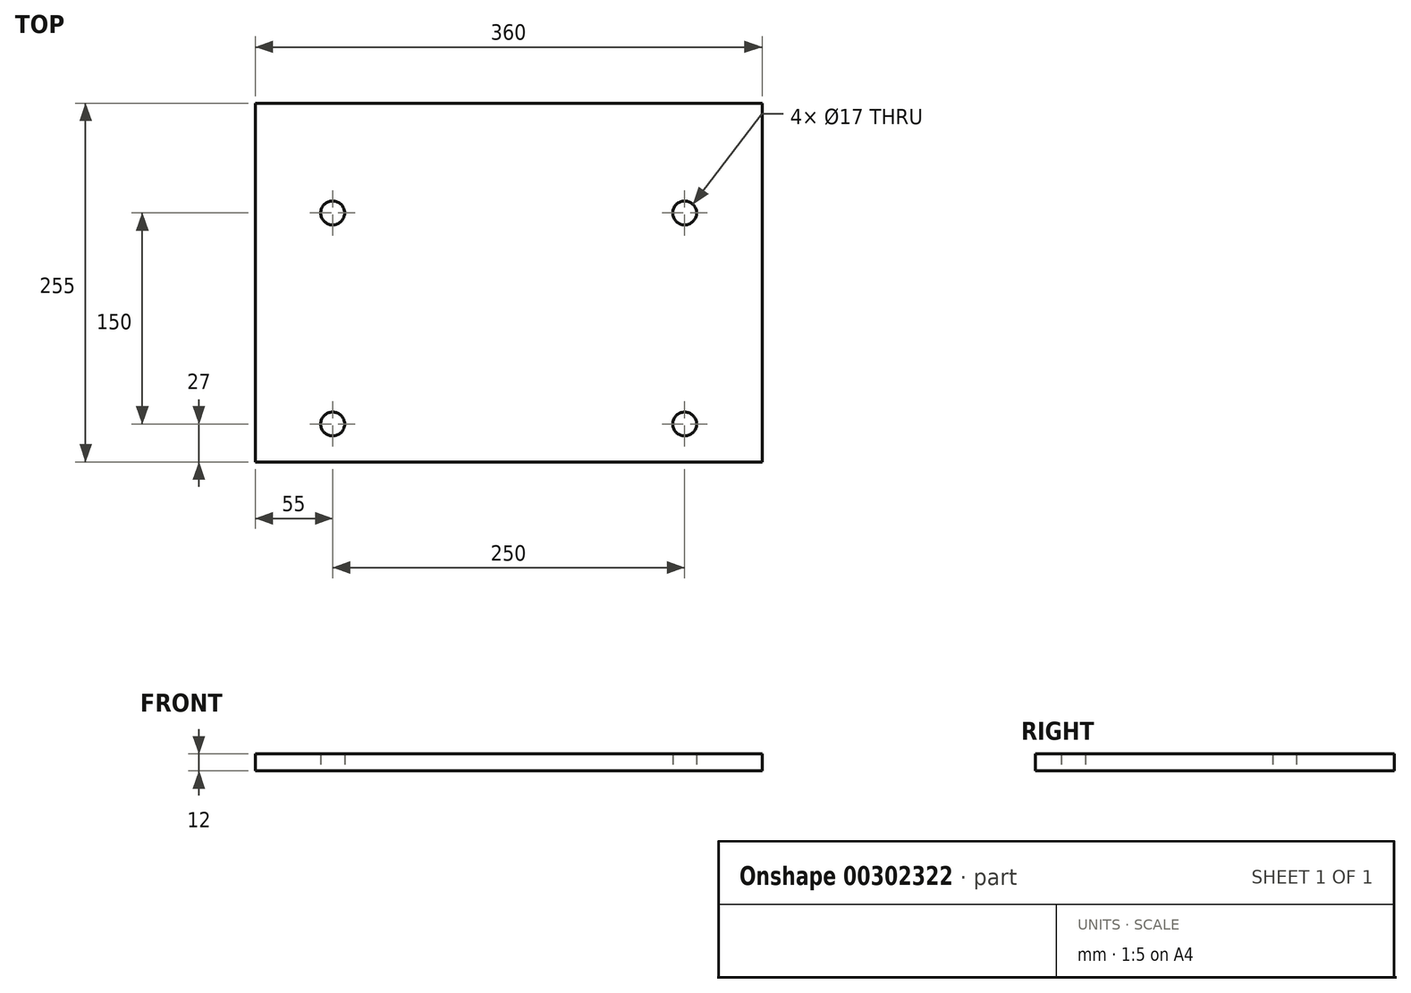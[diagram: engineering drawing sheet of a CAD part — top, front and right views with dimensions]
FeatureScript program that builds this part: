
annotation { "Feature Type Name" : "Feature", "Feature Type Description" : "" }
export const myFeature = defineFeature(function(context is Context, id is Id, definition is map)
    precondition{}
    {
        {
            var Q0;
            Q0=qCreatedBy(makeId("Top.planeOp"),FACE);
            var sketch = newSketch(context, id + "F0", { "sketchPlane" : qUnion([Q0])});
            skLineSegment(sketch, "E0.bottom", {"start": v(0, 0) * mm, "end": v(360, 0) * mm});
            skLineSegment(sketch, "E0.top", {"start": v(0, 255) * mm, "end": v(360, 255) * mm});
            skLineSegment(sketch, "E0.left", {"start": v(0, 0) * mm, "end": v(0, 255) * mm});
            skLineSegment(sketch, "E0.right", {"start": v(360, 0) * mm, "end": v(360, 255) * mm});
            skLineSegment(sketch, "E1", {"start": v(180, 295.6) * mm, "end": v(180, -60.75) * mm});
            skCircle(sketch, "E2", {"center": v(305, 177) * mm, "radius": 8.5 * mm});
            skCircle(sketch, "E3", {"center": v(305, 27) * mm, "radius": 8.5 * mm});
            skCircle(sketch, "E4.MirrorC", {"center": v(55, 177) * mm, "radius": 8.5 * mm});
            skCircle(sketch, "E5.MirrorC", {"center": v(55, 27) * mm, "radius": 8.5 * mm});
            skSolve(sketch);
        }
        {
            var Q0;
            Q0 = qSketchRegion(id + "F0", true);
            extrude(context, id + "F1", {"entities" : qUnion([Q0]), "depth" : 12 * mm});
        }
    });
